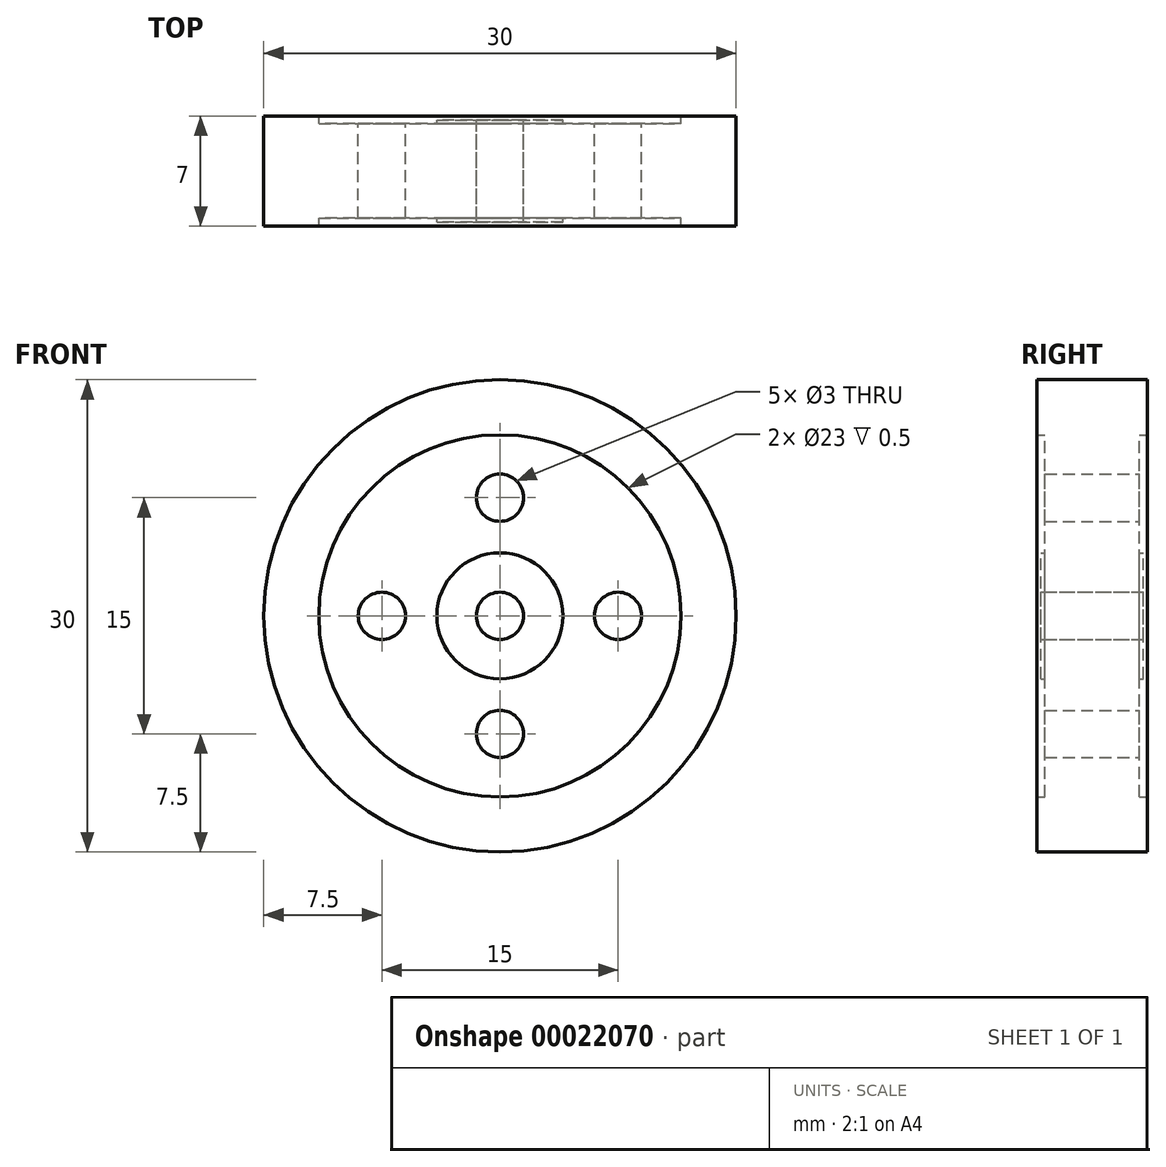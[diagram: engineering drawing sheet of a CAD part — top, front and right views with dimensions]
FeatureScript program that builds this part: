
annotation { "Feature Type Name" : "Feature", "Feature Type Description" : "" }
export const myFeature = defineFeature(function(context is Context, id is Id, definition is map)
    precondition{}
    {
        {
            var Q0;
            Q0=qCreatedBy(makeId("Front.planeOp"),FACE);
            var sketch = newSketch(context, id + "F0", { "sketchPlane" : qUnion([Q0])});
            skCircle(sketch, "E0", {"center": v(0, 0) * mm, "radius": 15 * mm});
            skCircle(sketch, "E1", {"center": v(0, 0) * mm, "radius": 4 * mm});
            skCircle(sketch, "E2", {"center": v(0, 0) * mm, "radius": 1.5 * mm});
            skCircle(sketch, "E3", {"center": v(0, 7.5) * mm, "radius": 1.5 * mm});
            skCircle(sketch, "E4.1.0", {"center": v(-7.5, 0) * mm, "radius": 1.5 * mm});
            skCircle(sketch, "E4.2.0", {"center": v(0, -7.5) * mm, "radius": 1.5 * mm});
            skCircle(sketch, "E4.3.0", {"center": v(7.5, 0) * mm, "radius": 1.5 * mm});
            skCircle(sketch, "E5", {"center": v(0, 0) * mm, "radius": 11.5 * mm});
            skSolve(sketch);
        }
        {
            var Q0;
            Q0=makeQuery(id+"F0.imprint","IMPRINT",FACE,{"disambiguationData":[TD([[makeQuery(id+"F0.imprint","IMPRINT",EDGE,{"derivedFrom":sQuery(id+"F0.wireOp",EDGE,"E1")}),1.0]])]});
            extrude(context, id + "F1", {"entities" : qUnion([Q0]), "endBound" : BoundingType.SYMMETRIC, "depth" : 6.5 * mm});
        }
        {
            var Q0;
            Q0=makeQuery(id+"F0.imprint","IMPRINT",FACE,{"disambiguationData":[TD([[makeQuery(id+"F0.imprint","IMPRINT",EDGE,{"derivedFrom":sQuery(id+"F0.wireOp",EDGE,"E1")}),-1.0]])]});
            extrude(context, id + "F2", {"entities" : qUnion([Q0]), "operationType" : NewBodyOperationType.ADD, "endBound" : BoundingType.SYMMETRIC, "depth" : 6 * mm});
        }
        {
            var Q0;
            Q0=qSketchRegion(id+"F0",true);
            extrude(context, id + "F3", {"entities" : qUnion([Q0]), "operationType" : NewBodyOperationType.ADD, "endBound" : BoundingType.SYMMETRIC, "depth" : 7 * mm});
        }
    });
